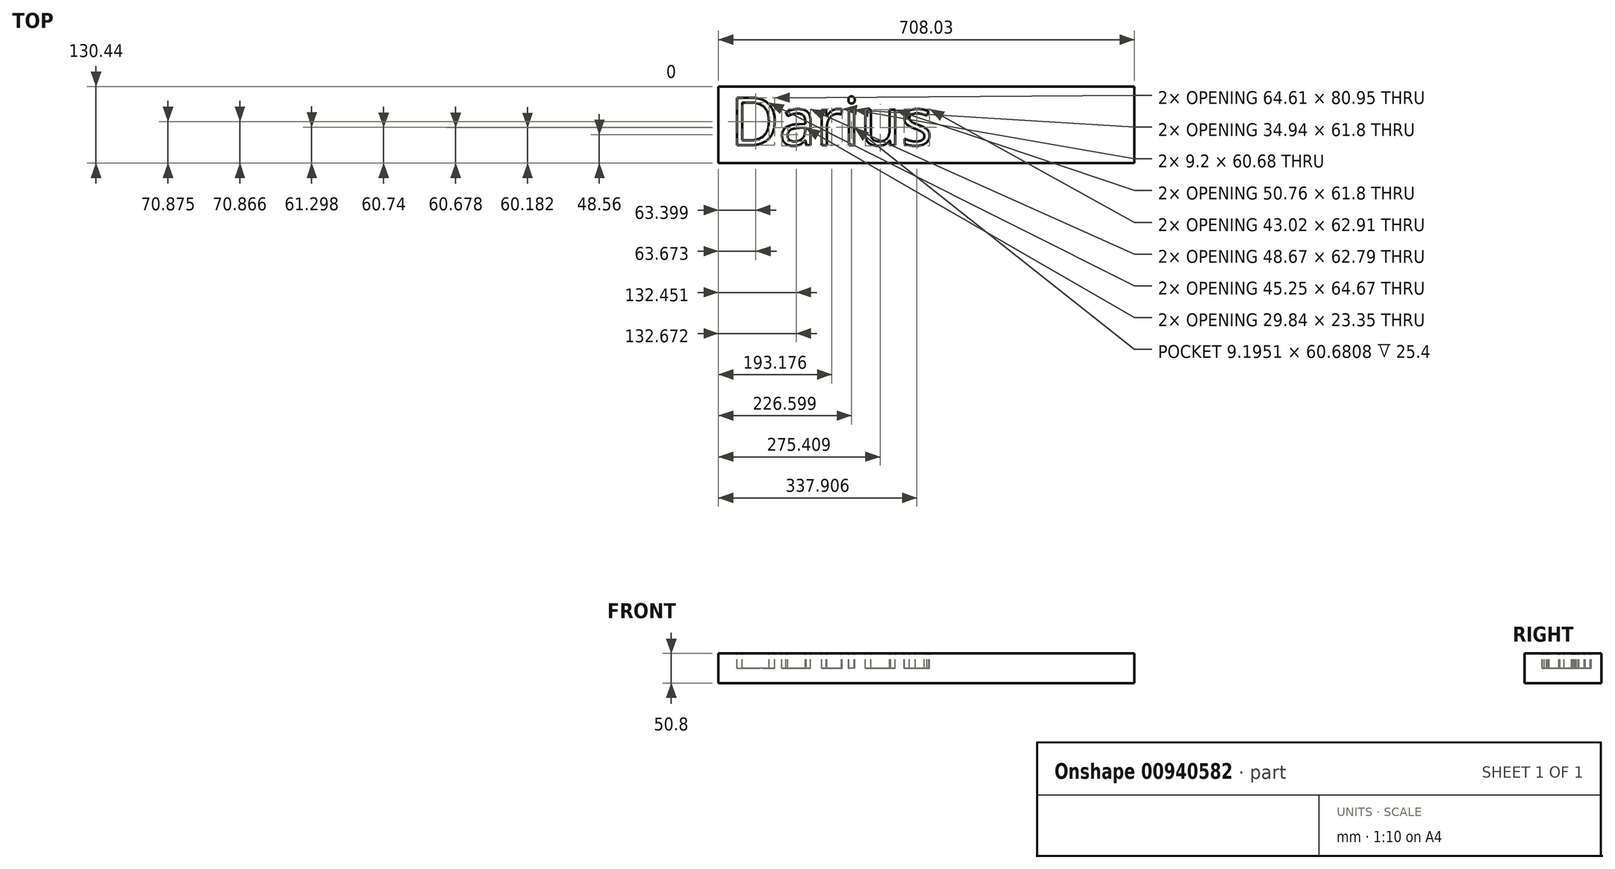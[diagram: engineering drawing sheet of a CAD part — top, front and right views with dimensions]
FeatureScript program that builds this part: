
annotation { "Feature Type Name" : "Feature", "Feature Type Description" : "" }
export const myFeature = defineFeature(function(context is Context, id is Id, definition is map)
    precondition{}
    {
        {
            var Q0;
            Q0=qCreatedBy(makeId("Top.planeOp"),FACE);
            var sketch = newSketch(context, id + "F0", { "sketchPlane" : qUnion([Q0])});
            skLineSegment(sketch, "E0.bottom", {"start": v(-127.53, -220.04) * mm, "end": v(580.5, -220.04) * mm});
            skLineSegment(sketch, "E0.top", {"start": v(-127.53, -350.48) * mm, "end": v(580.5, -350.48) * mm});
            skLineSegment(sketch, "E0.left", {"start": v(-127.53, -220.04) * mm, "end": v(-127.53, -350.48) * mm});
            skLineSegment(sketch, "E0.right", {"start": v(580.5, -220.04) * mm, "end": v(580.5, -350.48) * mm});
            skSolve(sketch);
        }
        {
            var Q0;
            Q0=makeQuery(id+"F0.imprint","IMPRINT",FACE,{"disambiguationData":[TD([[makeQuery(id+"F0.imprint","IMPRINT",EDGE,{"derivedFrom":sQuery(id+"F0.wireOp",EDGE,"E0.bottom")}),-1.0]])]});
            extrude(context, id + "F1", {"entities" : qUnion([Q0]), "oppositeDirection" : true, "depth" : 50.8 * mm, "offsetDistance" : 25.4 * mm});
        }
        {
            var Q0;
            Q0=qCreatedBy(makeId("Top.planeOp"),FACE);
            var sketch = newSketch(context, id + "F2", { "sketchPlane" : qUnion([Q0])});
            skText(sketch, "E1", { "text": "Darius", "fontName": "OpenSans-Regular.ttf"});
            const initialGuessF2  = {"E1": [-0.10729, -0.32008, 1, 0, 0.08164]};
            skSetInitialGuess(sketch, initialGuessF2);
            skSolve(sketch);
        }
        {
            var Q0;
            Q0 = qSketchRegion(id + "F2", true);
            extrude(context, id + "F3", {"entities" : qUnion([Q0]), "operationType" : NewBodyOperationType.REMOVE, "oppositeDirection" : true, "depth" : 25.4 * mm, "offsetDistance" : 25.4 * mm});
        }
    });
